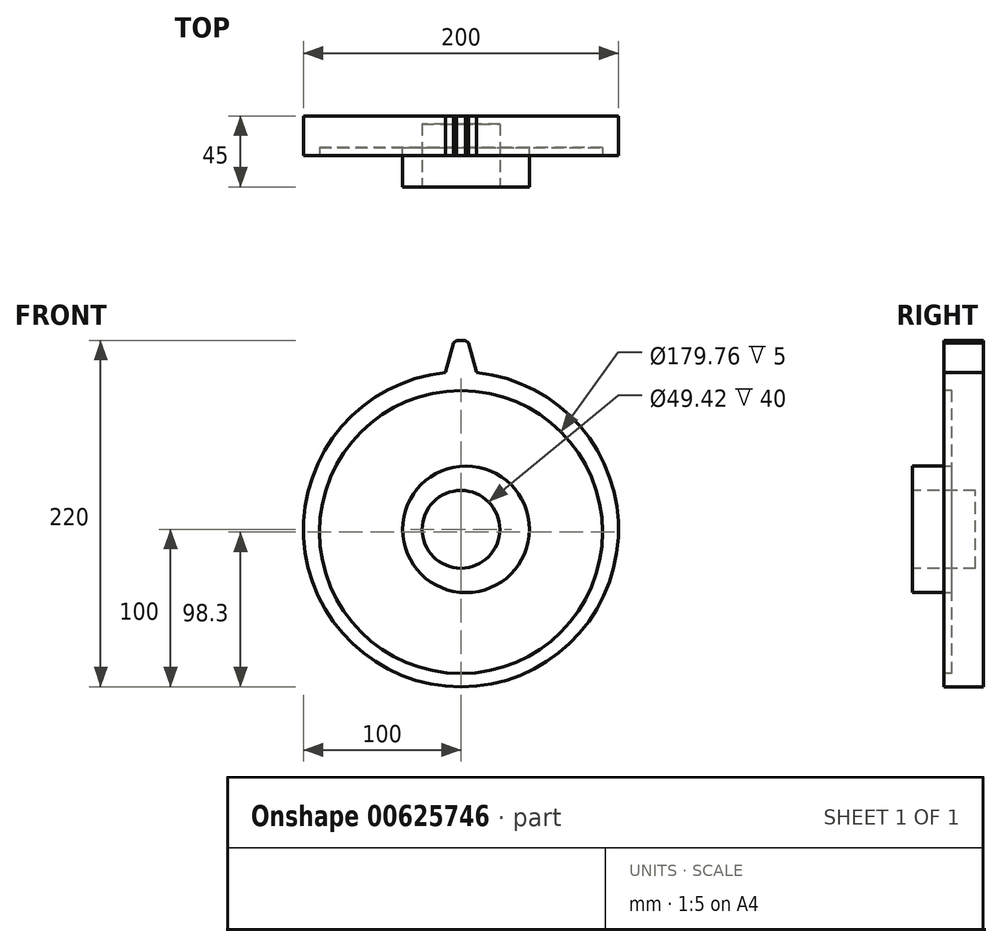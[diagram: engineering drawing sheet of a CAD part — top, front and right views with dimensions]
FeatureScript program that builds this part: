
annotation { "Feature Type Name" : "Feature", "Feature Type Description" : "" }
export const myFeature = defineFeature(function(context is Context, id is Id, definition is map)
    precondition{}
    {
        {
            var Q0;
            Q0=qCreatedBy(makeId("Front.planeOp"),FACE);
            var sketch = newSketch(context, id + "F0", { "sketchPlane" : qUnion([Q0])});
            skCircle(sketch, "E0", {"center": v(0, 0) * mm, "radius": 100 * mm});
            skSolve(sketch);
        }
        {
            var Q0;
            Q0=makeQuery(id+"F0.imprint","IMPRINT",FACE,{"disambiguationData":[TD([[makeQuery(id+"F0.imprint","IMPRINT",EDGE,{"derivedFrom":sQuery(id+"F0.wireOp",EDGE,"E0")}),1.0]])]});
            extrude(context, id + "F1", {"entities" : qUnion([Q0]), "depth" : 25 * mm, "offsetDistance" : 25 * mm});
        }
        {
            var Q0;
            Q0=qCreatedBy(makeId("Front.planeOp"),FACE);
            var sketch = newSketch(context, id + "F2", { "sketchPlane" : qUnion([Q0])});
            skLineSegment(sketch, "E1", {"start": v(-10, 99.5) * mm, "end": v(-4.5, 120) * mm});
            skLineSegment(sketch, "E2", {"start": v(-4.5, 120) * mm, "end": v(4.5, 120) * mm});
            skLineSegment(sketch, "E3", {"start": v(4.5, 120) * mm, "end": v(10, 99.5) * mm});
            skLineSegment(sketch, "E4", {"start": v(10, 99.5) * mm, "end": v(-10, 99.5) * mm});
            skSolve(sketch);
        }
        {
            var Q0;
            Q0=makeQuery(id+"F2.imprint","IMPRINT",FACE,{"disambiguationData":[TD([[makeQuery(id+"F2.imprint","IMPRINT",EDGE,{"derivedFrom":sQuery(id+"F2.wireOp",EDGE,"E1")}),-1.0]])]});
            extrude(context, id + "F3", {"entities" : qUnion([Q0]), "operationType" : NewBodyOperationType.ADD, "depth" : 25 * mm, "offsetDistance" : 25 * mm});
        }
        {
            var Q0;
            Q0=makeQuery(id+"F3.opExtrude","SWEPT_EDGE",EDGE,{"disambiguationData":[OSD([sQuery(id+"F2.wireOp",EDGE,"E2"),sQuery(id+"F2.wireOp",EDGE,"E3")])]});
            var Q1;
            Q1=makeQuery(id+"F3.opExtrude","SWEPT_EDGE",EDGE,{"disambiguationData":[OSD([sQuery(id+"F2.wireOp",EDGE,"E1"),sQuery(id+"F2.wireOp",EDGE,"E2")])]});
            chamfer(context, id + "F4", {"entities" : qUnion([Q0, Q1]), "width" : 2 * mm, "tangentPropagation" : true});
        }
        {
            var Q0;
            Q0=makeQuery(id+"F3.opExtrude","SWEPT_EDGE",EDGE,{"disambiguationData":[OSD([sQuery(id+"F2.wireOp",EDGE,"E3"),sQuery(id+"F2.wireOp",EDGE,"E4")])]});
            var Q1;
            Q1=makeQuery(id+"F3.opExtrude","SWEPT_EDGE",EDGE,{"disambiguationData":[OSD([sQuery(id+"F2.wireOp",EDGE,"E1"),sQuery(id+"F2.wireOp",EDGE,"E4")])]});
            fillet(context, id + "F5", {"entities" : qUnion([Q0, Q1]), "radius" : 5 * mm, "tangentPropagation" : true, "allowEdgeOverflow" : false});
        }
        {
            var Q0;
            {var subQ0=sQuery(id+"F2.wireOp",EDGE,"E4");var subQ1=sQuery(id+"F2.wireOp",EDGE,"E3");var subQ2=sQuery(id+"F2.wireOp",EDGE,"E2");var subQ3=sQuery(id+"F2.wireOp",EDGE,"E1");Q0=makeQuery(id+"FfQ11RXKx6o07uQ_1.19.F3.boolean.opBoolean","MERGE",FACE,{"derivedFrom":[makeQuery(id+"FfQ11RXKx6o07uQ_1.18.F3.boolean.opBoolean","MERGE",FACE,{"derivedFrom":[makeQuery(id+"FfQ11RXKx6o07uQ_1.17.F3.boolean.opBoolean","MERGE",FACE,{"derivedFrom":[makeQuery(id+"FfQ11RXKx6o07uQ_1.16.F3.boolean.opBoolean","MERGE",FACE,{"derivedFrom":[makeQuery(id+"FfQ11RXKx6o07uQ_1.15.F3.boolean.opBoolean","MERGE",FACE,{"derivedFrom":[makeQuery(id+"FfQ11RXKx6o07uQ_1.14.F3.boolean.opBoolean","MERGE",FACE,{"derivedFrom":[makeQuery(id+"FfQ11RXKx6o07uQ_1.13.F3.boolean.opBoolean","MERGE",FACE,{"derivedFrom":[makeQuery(id+"FfQ11RXKx6o07uQ_1.12.F3.boolean.opBoolean","MERGE",FACE,{"derivedFrom":[makeQuery(id+"FfQ11RXKx6o07uQ_1.11.F3.boolean.opBoolean","MERGE",FACE,{"derivedFrom":[makeQuery(id+"FfQ11RXKx6o07uQ_1.10.F3.boolean.opBoolean","MERGE",FACE,{"derivedFrom":[makeQuery(id+"FfQ11RXKx6o07uQ_1.9.F3.boolean.opBoolean","MERGE",FACE,{"derivedFrom":[makeQuery(id+"FfQ11RXKx6o07uQ_1.8.F3.boolean.opBoolean","MERGE",FACE,{"derivedFrom":[makeQuery(id+"FfQ11RXKx6o07uQ_1.7.F3.boolean.opBoolean","MERGE",FACE,{"derivedFrom":[makeQuery(id+"FfQ11RXKx6o07uQ_1.6.F3.boolean.opBoolean","MERGE",FACE,{"derivedFrom":[makeQuery(id+"FfQ11RXKx6o07uQ_1.5.F3.boolean.opBoolean","MERGE",FACE,{"derivedFrom":[makeQuery(id+"FfQ11RXKx6o07uQ_1.4.F3.boolean.opBoolean","MERGE",FACE,{"derivedFrom":[makeQuery(id+"FfQ11RXKx6o07uQ_1.3.F3.boolean.opBoolean","MERGE",FACE,{"derivedFrom":[makeQuery(id+"FfQ11RXKx6o07uQ_1.2.F3.boolean.opBoolean","MERGE",FACE,{"derivedFrom":[makeQuery(id+"FfQ11RXKx6o07uQ_1.1.F3.boolean.opBoolean","MERGE",FACE,{"derivedFrom":[makeQuery(id+"F3.boolean.opBoolean","MERGE",FACE,{"derivedFrom":[makeQuery(id+"F1.opExtrude","CAP_FACE",FACE,{"disambiguationData":[OSD([sQuery(id+"F0.wireOp",EDGE,"E0")])],"isStart":false}),makeQuery(id+"F3.opExtrude","CAP_FACE",FACE,{"disambiguationData":[OSD([subQ3,subQ2,subQ1,subQ0])],"isStart":false})]}),makeQuery(id+"FfQ11RXKx6o07uQ_1.1.F3.opExtrude","CAP_FACE",FACE,{"disambiguationData":[OSD([subQ3,subQ2,subQ1,subQ0])],"isStart":false})]}),makeQuery(id+"FfQ11RXKx6o07uQ_1.2.F3.opExtrude","CAP_FACE",FACE,{"disambiguationData":[OSD([subQ3,subQ2,subQ1,subQ0])],"isStart":false})]}),makeQuery(id+"FfQ11RXKx6o07uQ_1.3.F3.opExtrude","CAP_FACE",FACE,{"disambiguationData":[OSD([subQ3,subQ2,subQ1,subQ0])],"isStart":false})]}),makeQuery(id+"FfQ11RXKx6o07uQ_1.4.F3.opExtrude","CAP_FACE",FACE,{"disambiguationData":[OSD([subQ3,subQ2,subQ1,subQ0])],"isStart":false})]}),makeQuery(id+"FfQ11RXKx6o07uQ_1.5.F3.opExtrude","CAP_FACE",FACE,{"disambiguationData":[OSD([subQ3,subQ2,subQ1,subQ0])],"isStart":false})]}),makeQuery(id+"FfQ11RXKx6o07uQ_1.6.F3.opExtrude","CAP_FACE",FACE,{"disambiguationData":[OSD([subQ3,subQ2,subQ1,subQ0])],"isStart":false})]}),makeQuery(id+"FfQ11RXKx6o07uQ_1.7.F3.opExtrude","CAP_FACE",FACE,{"disambiguationData":[OSD([subQ3,subQ2,subQ1,subQ0])],"isStart":false})]}),makeQuery(id+"FfQ11RXKx6o07uQ_1.8.F3.opExtrude","CAP_FACE",FACE,{"disambiguationData":[OSD([subQ3,subQ2,subQ1,subQ0])],"isStart":false})]}),makeQuery(id+"FfQ11RXKx6o07uQ_1.9.F3.opExtrude","CAP_FACE",FACE,{"disambiguationData":[OSD([subQ3,subQ2,subQ1,subQ0])],"isStart":false})]}),makeQuery(id+"FfQ11RXKx6o07uQ_1.10.F3.opExtrude","CAP_FACE",FACE,{"disambiguationData":[OSD([subQ3,subQ2,subQ1,subQ0])],"isStart":false})]}),makeQuery(id+"FfQ11RXKx6o07uQ_1.11.F3.opExtrude","CAP_FACE",FACE,{"disambiguationData":[OSD([subQ3,subQ2,subQ1,subQ0])],"isStart":false})]}),makeQuery(id+"FfQ11RXKx6o07uQ_1.12.F3.opExtrude","CAP_FACE",FACE,{"disambiguationData":[OSD([subQ3,subQ2,subQ1,subQ0])],"isStart":false})]}),makeQuery(id+"FfQ11RXKx6o07uQ_1.13.F3.opExtrude","CAP_FACE",FACE,{"disambiguationData":[OSD([subQ3,subQ2,subQ1,subQ0])],"isStart":false})]}),makeQuery(id+"FfQ11RXKx6o07uQ_1.14.F3.opExtrude","CAP_FACE",FACE,{"disambiguationData":[OSD([subQ3,subQ2,subQ1,subQ0])],"isStart":false})]}),makeQuery(id+"FfQ11RXKx6o07uQ_1.15.F3.opExtrude","CAP_FACE",FACE,{"disambiguationData":[OSD([subQ3,subQ2,subQ1,subQ0])],"isStart":false})]}),makeQuery(id+"FfQ11RXKx6o07uQ_1.16.F3.opExtrude","CAP_FACE",FACE,{"disambiguationData":[OSD([subQ3,subQ2,subQ1,subQ0])],"isStart":false})]}),makeQuery(id+"FfQ11RXKx6o07uQ_1.17.F3.opExtrude","CAP_FACE",FACE,{"disambiguationData":[OSD([subQ3,subQ2,subQ1,subQ0])],"isStart":false})]}),makeQuery(id+"FfQ11RXKx6o07uQ_1.18.F3.opExtrude","CAP_FACE",FACE,{"disambiguationData":[OSD([subQ3,subQ2,subQ1,subQ0])],"isStart":false})]}),makeQuery(id+"FfQ11RXKx6o07uQ_1.19.F3.opExtrude","CAP_FACE",FACE,{"disambiguationData":[OSD([subQ3,subQ2,subQ1,subQ0])],"isStart":false})]});}
            var sketch = newSketch(context, id + "F6", { "sketchPlane" : qUnion([Q0])});
            skCircle(sketch, "E5", {"center": v(0, -1.7) * mm, "radius": 89.88 * mm});
            skSolve(sketch);
        }
        {
            var Q0;
            Q0=makeQuery(id+"F6.imprint","IMPRINT",FACE,{"disambiguationData":[TD([[makeQuery(id+"F6.imprint","IMPRINT",EDGE,{"derivedFrom":sQuery(id+"F6.wireOp",EDGE,"E5")}),1.0]])]});
            extrude(context, id + "F7", {"entities" : qUnion([Q0]), "operationType" : NewBodyOperationType.REMOVE, "oppositeDirection" : true, "depth" : 5 * mm, "offsetDistance" : 25 * mm});
        }
        {
            var Q0;
            Q0=makeQuery(id+"F7.boolean.opBoolean","COPY",FACE,{"derivedFrom":makeQuery(id+"F7.opExtrude","CAP_FACE",FACE,{"disambiguationData":[OSD([sQuery(id+"F6.wireOp",EDGE,"E5")])],"isStart":false})});
            var sketch = newSketch(context, id + "F8", { "sketchPlane" : qUnion([Q0])});
            skCircle(sketch, "E6", {"center": v(3.18, 0) * mm, "radius": 40.21 * mm});
            skSolve(sketch);
        }
        {
            var Q0;
            Q0=makeQuery(id+"F8.imprint","IMPRINT",FACE,{"disambiguationData":[TD([[makeQuery(id+"F8.imprint","IMPRINT",EDGE,{"derivedFrom":sQuery(id+"F8.wireOp",EDGE,"E6")}),1.0]])]});
            extrude(context, id + "F9", {"entities" : qUnion([Q0]), "operationType" : NewBodyOperationType.ADD, "depth" : 25 * mm, "offsetDistance" : 25 * mm});
        }
        {
            var Q0;
            Q0=makeQuery(id+"F9.opExtrude","CAP_FACE",FACE,{"disambiguationData":[OSD([sQuery(id+"F8.wireOp",EDGE,"E6")])],"isStart":false});
            var sketch = newSketch(context, id + "F10", { "sketchPlane" : qUnion([Q0])});
            skCircle(sketch, "E7", {"center": v(0, 0) * mm, "radius": 24.71 * mm});
            skSolve(sketch);
        }
        {
            var Q0;
            Q0=makeQuery(id+"F10.imprint","IMPRINT",FACE,{"disambiguationData":[TD([[makeQuery(id+"F10.imprint","IMPRINT",EDGE,{"derivedFrom":sQuery(id+"F10.wireOp",EDGE,"E7")}),1.0]])]});
            extrude(context, id + "F11", {"entities" : qUnion([Q0]), "operationType" : NewBodyOperationType.REMOVE, "oppositeDirection" : true, "depth" : 15 * mm, "offsetDistance" : 25 * mm});
        }
        {
            var Q0;
            Q0=makeQuery(id+"F11.boolean.opBoolean","COPY",FACE,{"derivedFrom":makeQuery(id+"F11.opExtrude","CAP_FACE",FACE,{"disambiguationData":[OSD([sQuery(id+"F10.wireOp",EDGE,"E7")])],"isStart":false})});
            extrude(context, id + "F12", {"entities" : qUnion([Q0]), "operationType" : NewBodyOperationType.REMOVE, "oppositeDirection" : true, "depth" : 25 * mm, "offsetDistance" : 25 * mm});
        }
    });
